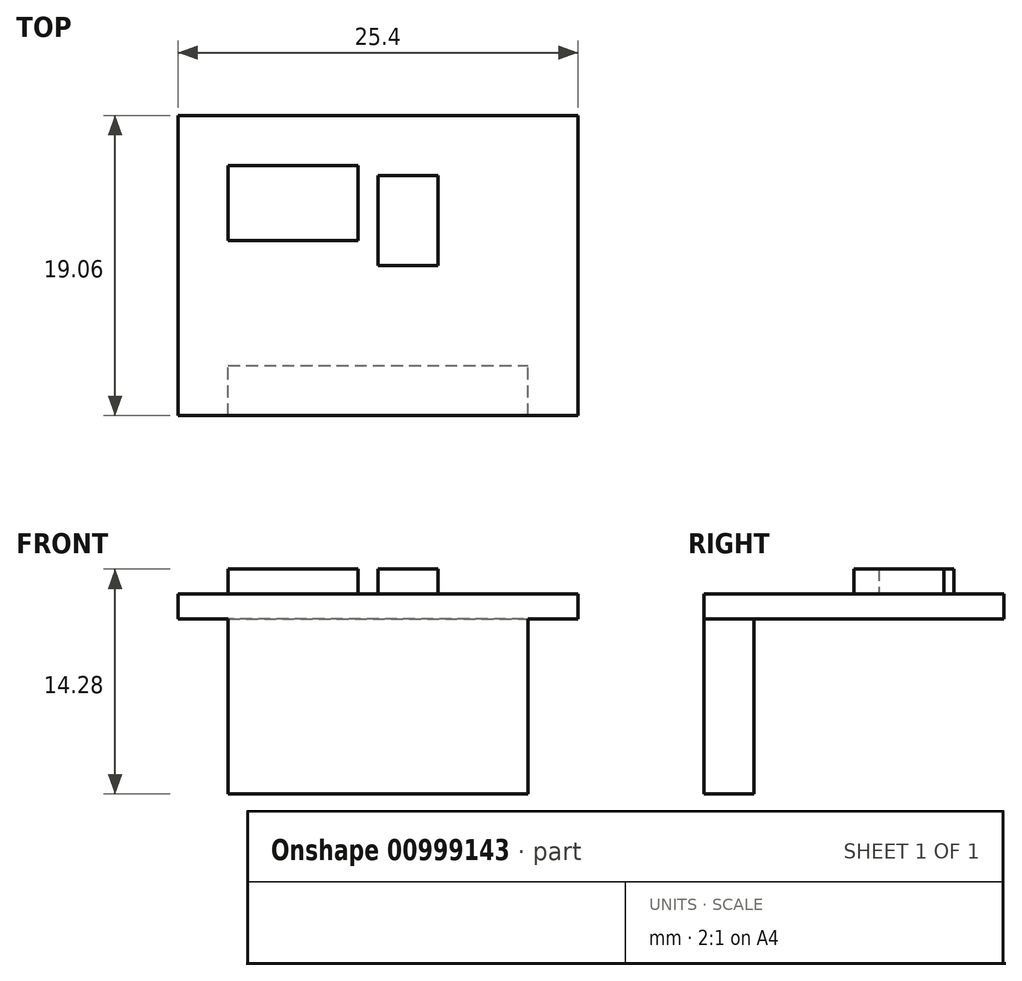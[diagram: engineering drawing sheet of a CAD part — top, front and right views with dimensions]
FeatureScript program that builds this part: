
annotation { "Feature Type Name" : "Feature", "Feature Type Description" : "" }
export const myFeature = defineFeature(function(context is Context, id is Id, definition is map)
    precondition{}
    {
        {
            var Q0;
            Q0=qCreatedBy(makeId("Top.planeOp"),FACE);
            var sketch = newSketch(context, id + "F0", { "sketchPlane" : qUnion([Q0])});
            skLineSegment(sketch, "E0.bottom", {"start": v(12.7, 9.53) * mm, "end": v(-12.7, 9.53) * mm});
            skLineSegment(sketch, "E0.top", {"start": v(12.7, -9.52) * mm, "end": v(-12.7, -9.52) * mm});
            skLineSegment(sketch, "E0.left", {"start": v(12.7, 9.53) * mm, "end": v(12.7, -9.52) * mm});
            skLineSegment(sketch, "E0.right", {"start": v(-12.7, 9.53) * mm, "end": v(-12.7, -9.52) * mm});
            skPoint(sketch, "E0.middle", {"position": v(0, 0) * mm});
            skLineSegment(sketch, "E1.bottom", {"start": v(-12.7, -9.52) * mm, "end": v(-9.53, -9.52) * mm});
            skLineSegment(sketch, "E1.top", {"start": v(-12.7, -6.35) * mm, "end": v(-9.53, -6.35) * mm});
            skLineSegment(sketch, "E1.left", {"start": v(-12.7, -9.52) * mm, "end": v(-12.7, -6.35) * mm});
            skLineSegment(sketch, "E1.right", {"start": v(-9.53, -9.52) * mm, "end": v(-9.53, -6.35) * mm});
            skLineSegment(sketch, "E2.bottom", {"start": v(12.7, -9.52) * mm, "end": v(9.53, -9.52) * mm});
            skLineSegment(sketch, "E2.top", {"start": v(12.7, -6.35) * mm, "end": v(9.53, -6.35) * mm});
            skLineSegment(sketch, "E2.left", {"start": v(12.7, -9.52) * mm, "end": v(12.7, -6.35) * mm});
            skLineSegment(sketch, "E2.right", {"start": v(9.53, -9.52) * mm, "end": v(9.53, -6.35) * mm});
            skLineSegment(sketch, "E3.bottom", {"start": v(-9.53, -6.35) * mm, "end": v(9.53, -6.35) * mm});
            skLineSegment(sketch, "E3.top", {"start": v(-9.53, -9.52) * mm, "end": v(9.53, -9.52) * mm});
            skLineSegment(sketch, "E3.left", {"start": v(-9.53, -6.35) * mm, "end": v(-9.53, -9.52) * mm});
            skLineSegment(sketch, "E3.right", {"start": v(9.53, -6.35) * mm, "end": v(9.53, -9.52) * mm});
            skLineSegment(sketch, "E4.top", {"start": v(-9.53, 9.53) * mm, "end": v(9.53, 9.53) * mm});
            skLineSegment(sketch, "E4.left", {"start": v(-9.53, -6.35) * mm, "end": v(-9.53, 9.53) * mm});
            skLineSegment(sketch, "E4.right", {"start": v(9.53, -6.35) * mm, "end": v(9.53, 9.53) * mm});
            skLineSegment(sketch, "E5.bottom", {"start": v(-9.53, 9.53) * mm, "end": v(-1.27, 9.53) * mm});
            skLineSegment(sketch, "E5.top", {"start": v(-9.53, 6.35) * mm, "end": v(-1.27, 6.35) * mm});
            skLineSegment(sketch, "E5.left", {"start": v(-9.53, 9.53) * mm, "end": v(-9.53, 6.35) * mm});
            skLineSegment(sketch, "E5.right", {"start": v(-1.27, 9.53) * mm, "end": v(-1.27, 6.35) * mm});
            skLineSegment(sketch, "E6.bottom", {"start": v(-1.27, 6.35) * mm, "end": v(-9.53, 6.35) * mm});
            skLineSegment(sketch, "E6.top", {"start": v(-1.27, 1.59) * mm, "end": v(-9.53, 1.59) * mm});
            skLineSegment(sketch, "E6.left", {"start": v(-1.27, 6.35) * mm, "end": v(-1.27, 1.59) * mm});
            skLineSegment(sketch, "E6.right", {"start": v(-9.53, 6.35) * mm, "end": v(-9.53, 1.59) * mm});
            skLineSegment(sketch, "E7.bottom", {"start": v(-1.27, 9.53) * mm, "end": v(3.8, 9.53) * mm});
            skLineSegment(sketch, "E7.top", {"start": v(-1.27, 5.72) * mm, "end": v(3.8, 5.72) * mm});
            skLineSegment(sketch, "E7.left", {"start": v(-1.27, 9.53) * mm, "end": v(-1.27, 5.72) * mm});
            skLineSegment(sketch, "E7.right", {"start": v(3.8, 9.53) * mm, "end": v(3.8, 5.72) * mm});
            skLineSegment(sketch, "E8.bottom", {"start": v(3.8, 5.72) * mm, "end": v(0, 5.72) * mm});
            skLineSegment(sketch, "E8.top", {"start": v(3.8, 0) * mm, "end": v(0, 0) * mm});
            skLineSegment(sketch, "E8.left", {"start": v(3.8, 5.72) * mm, "end": v(3.8, 0) * mm});
            skLineSegment(sketch, "E8.right", {"start": v(0, 5.72) * mm, "end": v(0, 0) * mm});
            skSolve(sketch);
        }
        {
            var Q0;
            {var subQ4=sQuery(id+"F0.wireOp",EDGE,"E1.top");Q0=makeQuery(id+"F0.imprint","IMPRINT",FACE,{"disambiguationData":[TD([[makeQuery(id+"F0.imprint","IMPRINT",EDGE,{"derivedFrom":subQ4}),-1.0]])]});}
            var Q1;
            {var subQ1=sQuery(id+"F0.wireOp",EDGE,"E1.top");Q1=makeQuery(id+"F0.imprint","IMPRINT",FACE,{"disambiguationData":[TD([[makeQuery(id+"F0.imprint","IMPRINT",EDGE,{"derivedFrom":subQ1}),1.0]])]});}
            var Q2;
            {var subQ8=sQuery(id+"F0.wireOp",EDGE,"E3.bottom");Q2=makeQuery(id+"F0.imprint","IMPRINT",FACE,{"disambiguationData":[TD([[makeQuery(id+"F0.imprint","IMPRINT",EDGE,{"derivedFrom":subQ8}),1.0]])]});}
            var Q3;
            {var subQ4=sQuery(id+"F0.wireOp",EDGE,"E5.top");Q3=makeQuery(id+"F0.imprint","IMPRINT",FACE,{"disambiguationData":[TD([[makeQuery(id+"F0.imprint","IMPRINT",EDGE,{"derivedFrom":subQ4}),1.0]])]});}
            var Q4;
            {var subQ4=sQuery(id+"F0.wireOp",EDGE,"E5.right");Q4=makeQuery(id+"F0.imprint","IMPRINT",FACE,{"disambiguationData":[TD([[makeQuery(id+"F0.imprint","IMPRINT",EDGE,{"derivedFrom":subQ4}),1.0]])]});}
            var Q5;
            {var subQ4=sQuery(id+"F0.wireOp",EDGE,"E2.top");Q5=makeQuery(id+"F0.imprint","IMPRINT",FACE,{"disambiguationData":[TD([[makeQuery(id+"F0.imprint","IMPRINT",EDGE,{"derivedFrom":subQ4}),-1.0]])]});}
            var Q6;
            {var subQ4=sQuery(id+"F0.wireOp",EDGE,"E2.top");Q6=makeQuery(id+"F0.imprint","IMPRINT",FACE,{"disambiguationData":[TD([[makeQuery(id+"F0.imprint","IMPRINT",EDGE,{"derivedFrom":subQ4}),1.0]])]});}
            extrude(context, id + "F1", {"entities" : qUnion([Q0, Q1, Q2, Q3, Q4, Q5, Q6]), "depth" : 1.59 * mm, "offsetDistance" : 25.4 * mm});
        }
        {
            var Q0;
            {var subQ3=sQuery(id+"F0.wireOp",EDGE,"E5.top");Q0=makeQuery(id+"F0.imprint","IMPRINT",FACE,{"disambiguationData":[TD([[makeQuery(id+"F0.imprint","IMPRINT",EDGE,{"derivedFrom":subQ3}),-1.0]])]});}
            var Q1;
            Q1=makeQuery(id+"F0.imprint","IMPRINT",FACE,{"disambiguationData":[TD([[makeQuery(id+"F0.imprint","IMPRINT",EDGE,{"derivedFrom":sQuery(id+"F0.wireOp",EDGE,"E8.top")}),-1.0]])]});
            extrude(context, id + "F2", {"entities" : qUnion([Q0, Q1]), "operationType" : NewBodyOperationType.ADD, "depth" : 3.17 * mm, "offsetDistance" : 25.4 * mm});
        }
        {
            var Q0;
            {var subQ2=sQuery(id+"F0.wireOp",EDGE,"E1.right");Q0=makeQuery(id+"F0.imprint","IMPRINT",FACE,{"disambiguationData":[TD([[makeQuery(id+"F0.imprint","IMPRINT",EDGE,{"derivedFrom":subQ2}),-1.0]])]});}
            extrude(context, id + "F3", {"entities" : qUnion([Q0]), "operationType" : NewBodyOperationType.ADD, "depth" : 1.59 * mm, "offsetDistance" : 25.4 * mm});
        }
        {
            var Q0;
            {var subQ2=sQuery(id+"F0.wireOp",EDGE,"E1.right");Q0=makeQuery(id+"F0.imprint","IMPRINT",FACE,{"disambiguationData":[TD([[makeQuery(id+"F0.imprint","IMPRINT",EDGE,{"derivedFrom":subQ2}),-1.0]])]});}
            extrude(context, id + "F4", {"entities" : qUnion([Q0]), "operationType" : NewBodyOperationType.ADD, "oppositeDirection" : true, "depth" : 11.1 * mm, "offsetDistance" : 25.4 * mm});
        }
    });
